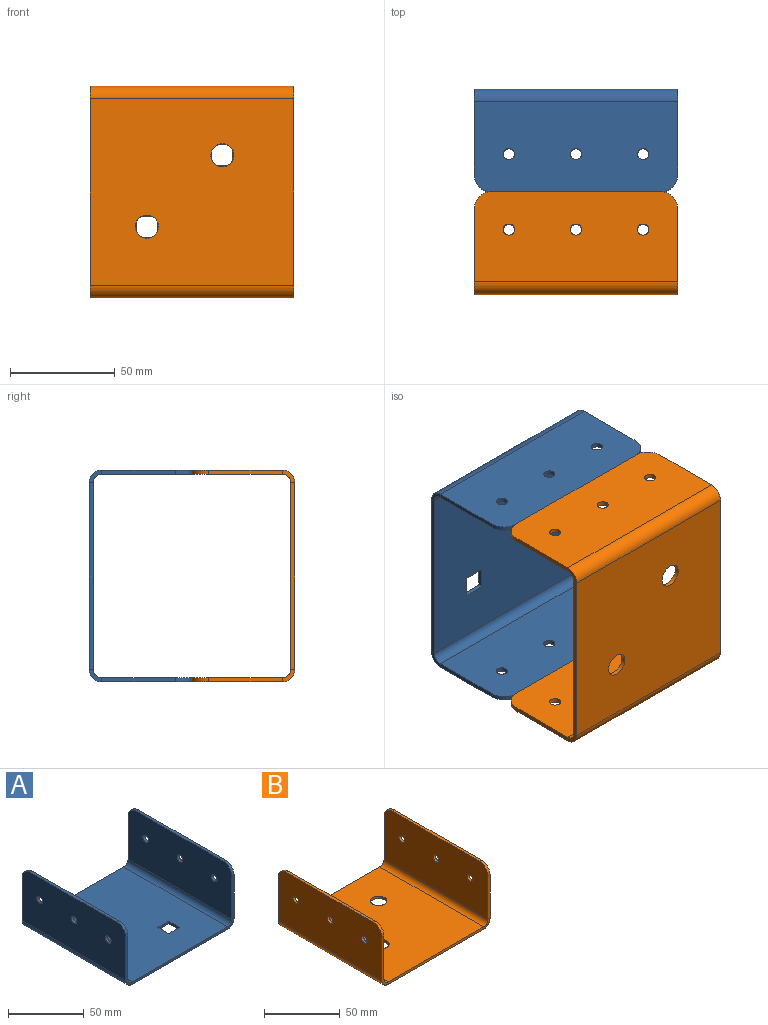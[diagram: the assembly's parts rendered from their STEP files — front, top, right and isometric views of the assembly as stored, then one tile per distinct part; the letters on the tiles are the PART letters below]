
ASSEMBLY  parts=2 mates=1
PART A: 40 faces, bbox 101x97x49 mm
  f0: plane 89x2mm, normal (0,-1,0), area 178mm2, adj f10,f11,f23,f37
  f1: plane 10.1x2mm, normal (0,1,0), area 20.2mm2, adj f2,f8,f10,f11
  f2: plane 10.1x2mm, normal (-1,0,0), area 20.2mm2, adj f1,f3,f10,f11
  f3: plane 10.1x2mm, normal (0,-1,0), area 20.2mm2, adj f2,f8,f10,f11
  f4: plane 10.1x2mm, normal (-1,0,0), area 20.2mm2, adj f5,f7,f10,f11
  f5: plane 10.1x2mm, normal (0,-1,0), area 20.2mm2, adj f4,f6,f10,f11
  f6: plane 10.1x2mm, normal (1,0,0), area 20.2mm2, adj f5,f7,f10,f11
  f7: plane 10.1x2mm, normal (0,1,0), area 20.2mm2, adj f4,f6,f10,f11
  f8: plane 10.1x2mm, normal (1,0,0), area 20.2mm2, adj f1,f3,f10,f11
  f9: plane 89x2mm, normal (0,1,0), area 178mm2, adj f10,f11,f22,f36
  f10: plane 97x89mm, normal (0,0,-1), area 8429mm2, adj f0,f1,f2,f3,f4,f5,f6,f7
  f11: plane 97x89mm, normal (0,0,1), area 8429mm2, adj f0,f1,f2,f3,f4,f5,f6,f7
  f12: plane 81x2mm, normal (0,0,1), area 162mm2, adj f18,f19,f20,f21
  f13: plane 35x2mm, normal (0,1,0), area 70mm2, adj f18,f19,f21,f22
  f14: cylinder r=2.65mm len=5.3mm, axis (-1,0,0), area 33.3mm2, adj f18,f19
  f15: cylinder r=2.65mm len=5.3mm, axis (-1,0,0), area 33.3mm2, adj f18,f19
  f16: cylinder r=2.65mm len=5.3mm, axis (-1,0,0), area 33.3mm2, adj f18,f19
  f17: plane 35x2mm, normal (0,-1,0), area 70mm2, adj f18,f19,f20,f23
  f18: plane 97x43mm, normal (-1,0,0), area 4077.3mm2, adj f12,f13,f14,f15,f16,f17,f20,f21
  f19: plane 97x43mm, normal (1,0,0), area 4077.3mm2, adj f12,f13,f14,f15,f16,f17,f20,f21
  f20: cylinder r=8mm len=8mm, axis (-1,0,0), area 25.1mm2, adj f12,f17,f18,f19
  f21: cylinder r=8mm len=8mm, axis (-1,0,0), area 25.1mm2, adj f12,f13,f18,f19
  f22: plane 6x6mm, normal (0,1,0), area 15.7mm2, adj f9,f13,f24,f25
  f23: plane 6x6mm, normal (0,-1,0), area 15.7mm2, adj f0,f17,f24,f25
  f24: cylinder r=6mm len=97mm, axis (0,1,0), area 914.2mm2, adj f10,f18,f22,f23
  f25: cylinder r=4mm len=97mm, axis (0,1,0), area 609.5mm2, adj f11,f19,f22,f23
  f26: plane 81x2mm, normal (0,0,1), area 162mm2, adj f32,f33,f34,f35
  f27: plane 35x2mm, normal (0,-1,0), area 70mm2, adj f32,f33,f34,f37
  f28: cylinder r=2.65mm len=5.3mm, axis (1,0,0), area 33.3mm2, adj f32,f33
  f29: cylinder r=2.65mm len=5.3mm, axis (1,0,0), area 33.3mm2, adj f32,f33
  f30: cylinder r=2.65mm len=5.3mm, axis (1,0,0), area 33.3mm2, adj f32,f33
  f31: plane 35x2mm, normal (0,1,0), area 70mm2, adj f32,f33,f35,f36
  f32: plane 97x43mm, normal (1,0,0), area 4077.3mm2, adj f26,f27,f28,f29,f30,f31,f34,f35
  f33: plane 97x43mm, normal (-1,0,0), area 4077.3mm2, adj f26,f27,f28,f29,f30,f31,f34,f35
  f34: cylinder r=8mm len=8mm, axis (1,0,0), area 25.1mm2, adj f26,f27,f32,f33
  f35: cylinder r=8mm len=8mm, axis (1,0,0), area 25.1mm2, adj f26,f31,f32,f33
  f36: plane 6x6mm, normal (0,1,0), area 15.7mm2, adj f9,f31,f38,f39
  f37: plane 6x6mm, normal (0,-1,0), area 15.7mm2, adj f0,f27,f38,f39
  f38: cylinder r=6mm len=97mm, axis (0,1,0), area 914.2mm2, adj f10,f32,f36,f37
  f39: cylinder r=4mm len=97mm, axis (0,1,0), area 609.5mm2, adj f11,f33,f36,f37
PART B: 34 faces, bbox 101x97x49 mm
  f0: plane 89x2mm, normal (0,-1,0), area 178mm2, adj f4,f5,f17,f31
  f1: cylinder r=5.5mm len=11mm, axis (0,0,1), area 69.1mm2, adj f4,f5
  f2: cylinder r=5.5mm len=11mm, axis (0,0,1), area 69.1mm2, adj f4,f5
  f3: plane 89x2mm, normal (0,1,0), area 178mm2, adj f4,f5,f16,f30
  f4: plane 97x89mm, normal (0,0,-1), area 8442.9mm2, adj f0,f1,f2,f3,f18,f32
  f5: plane 97x89mm, normal (0,0,1), area 8442.9mm2, adj f0,f1,f2,f3,f19,f33
  f6: plane 81x2mm, normal (0,0,1), area 162mm2, adj f12,f13,f14,f15
  f7: plane 35x2mm, normal (0,1,0), area 70mm2, adj f12,f13,f15,f16
  f8: cylinder r=2.65mm len=5.3mm, axis (-1,0,0), area 33.3mm2, adj f12,f13
  f9: cylinder r=2.65mm len=5.3mm, axis (-1,0,0), area 33.3mm2, adj f12,f13
  f10: cylinder r=2.65mm len=5.3mm, axis (-1,0,0), area 33.3mm2, adj f12,f13
  f11: plane 35x2mm, normal (0,-1,0), area 70mm2, adj f12,f13,f14,f17
  f12: plane 97x43mm, normal (-1,0,0), area 4077.3mm2, adj f6,f7,f8,f9,f10,f11,f14,f15
  f13: plane 97x43mm, normal (1,0,0), area 4077.3mm2, adj f6,f7,f8,f9,f10,f11,f14,f15
  f14: cylinder r=8mm len=8mm, axis (-1,0,0), area 25.1mm2, adj f6,f11,f12,f13
  f15: cylinder r=8mm len=8mm, axis (-1,0,0), area 25.1mm2, adj f6,f7,f12,f13
  f16: plane 6x6mm, normal (0,1,0), area 15.7mm2, adj f3,f7,f18,f19
  f17: plane 6x6mm, normal (0,-1,0), area 15.7mm2, adj f0,f11,f18,f19
  f18: cylinder r=6mm len=97mm, axis (0,1,0), area 914.2mm2, adj f4,f12,f16,f17
  f19: cylinder r=4mm len=97mm, axis (0,1,0), area 609.5mm2, adj f5,f13,f16,f17
  f20: plane 81x2mm, normal (0,0,1), area 162mm2, adj f26,f27,f28,f29
  f21: plane 35x2mm, normal (0,-1,0), area 70mm2, adj f26,f27,f28,f31
  f22: cylinder r=2.65mm len=5.3mm, axis (1,0,0), area 33.3mm2, adj f26,f27
  f23: cylinder r=2.65mm len=5.3mm, axis (1,0,0), area 33.3mm2, adj f26,f27
  f24: cylinder r=2.65mm len=5.3mm, axis (1,0,0), area 33.3mm2, adj f26,f27
  f25: plane 35x2mm, normal (0,1,0), area 70mm2, adj f26,f27,f29,f30
  f26: plane 97x43mm, normal (1,0,0), area 4077.3mm2, adj f20,f21,f22,f23,f24,f25,f28,f29
  f27: plane 97x43mm, normal (-1,0,0), area 4077.3mm2, adj f20,f21,f22,f23,f24,f25,f28,f29
  f28: cylinder r=8mm len=8mm, axis (1,0,0), area 25.1mm2, adj f20,f21,f26,f27
  f29: cylinder r=8mm len=8mm, axis (1,0,0), area 25.1mm2, adj f20,f25,f26,f27
  f30: plane 6x6mm, normal (0,1,0), area 15.7mm2, adj f3,f25,f32,f33
  f31: plane 6x6mm, normal (0,-1,0), area 15.7mm2, adj f0,f21,f32,f33
  f32: cylinder r=6mm len=97mm, axis (0,1,0), area 914.2mm2, adj f4,f26,f30,f31
  f33: cylinder r=4mm len=97mm, axis (0,1,0), area 609.5mm2, adj f5,f27,f30,f31
PLACE A rot(axis=(0.58,0.58,-0.58),120deg) t=(-47.71,49.56,39.2)mm fixed
PLACE B rot(axis=(-0.58,0.58,0.58),120deg) t=(49.29,-48.44,39.2)mm
MATE revolute B.f6 <-> A.f12  axis (0,1,0) through (0.79,0.56,41.2)mm
